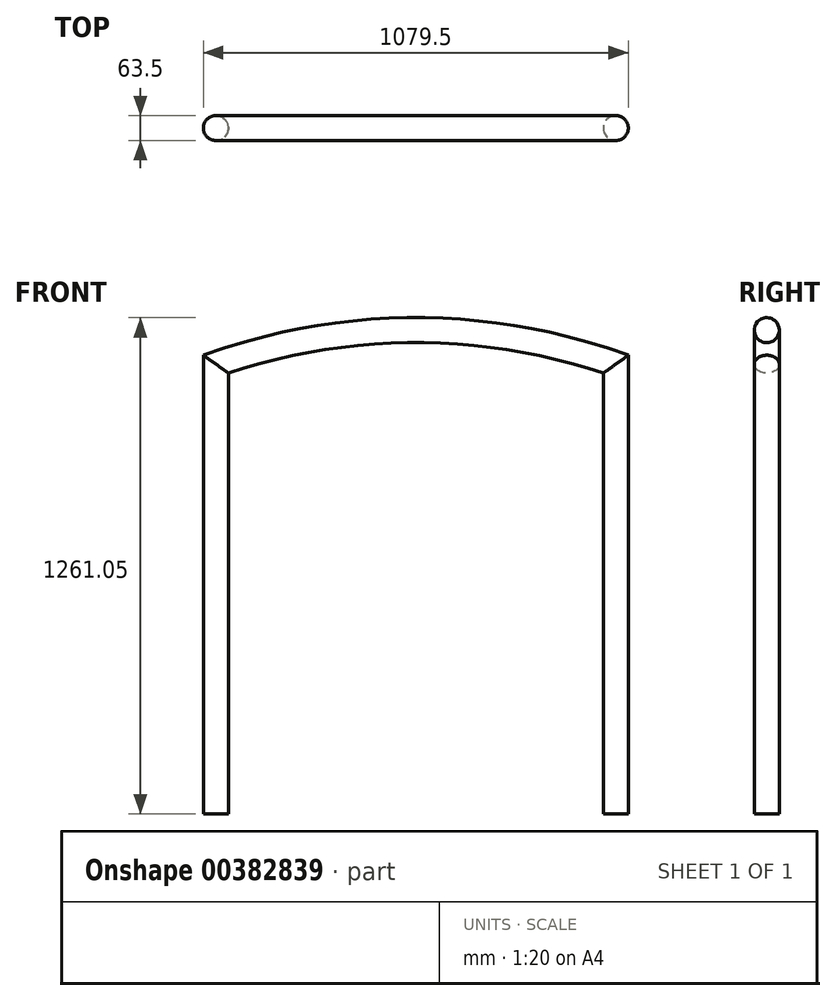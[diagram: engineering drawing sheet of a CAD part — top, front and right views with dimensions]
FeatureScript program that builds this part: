
annotation { "Feature Type Name" : "Feature", "Feature Type Description" : "" }
export const myFeature = defineFeature(function(context is Context, id is Id, definition is map)
    precondition{}
    {
        {
            var Q0;
            Q0=qCreatedBy(makeId("Front.planeOp"),FACE);
            var sketch = newSketch(context, id + "F0", { "sketchPlane" : qUnion([Q0])});
            skLineSegment(sketch, "E0", {"start": v(583.19, -789.06) * mm, "end": v(583.19, 353.94) * mm});
            skLineSegment(sketch, "E1", {"start": v(-432.81, -789.06) * mm, "end": v(-432.81, 353.94) * mm});
            skArc(sketch, "E2", {"start": v(583.19, 353.94) * mm, "mid": v(75.19, 440.24) * mm, "end": v(-432.81, 353.94) * mm});
            skSolve(sketch);
        }
        {
            var Q0;
            Q0=sQuery(id+"F0.wireOp",VERTEX,"E0.start");
            var Q1;
            Q1=sQuery(id+"F0.wireOp",EDGE,"E0");
            cPlane(context, id + "F1", {"entities" : qUnion([Q0, Q1]), "cplaneType" : CPlaneType.LINE_POINT, "offset" : 25.4 * mm, "width" : 152.4 * mm, "height" : 152.4 * mm});
        }
        {
            var Q0;
            Q0=qCreatedBy(id+"F1.planeOp",FACE);
            var sketch = newSketch(context, id + "F2", { "sketchPlane" : qUnion([Q0])});
            skPoint(sketch, "E3.0", {"position": v(583.19, 0) * mm});
            skCircle(sketch, "E4", {"center": v(583.19, 0) * mm, "radius": 31.75 * mm});
            skSolve(sketch);
        }
        {
            var Q0;
            Q0=makeQuery(id+"F2.imprint","IMPRINT",FACE,{"disambiguationData":[TD([[makeQuery(id+"F2.imprint","IMPRINT",EDGE,{"derivedFrom":sQuery(id+"F2.wireOp",EDGE,"E4")}),1.0]])]});
            var Q1;
            Q1=sQuery(id+"F0.wireOp",EDGE,"E0");
            var Q2;
            Q2=sQuery(id+"F0.wireOp",EDGE,"E2");
            var Q3;
            Q3=sQuery(id+"F0.wireOp",EDGE,"E1");
            sweep(context, id + "F3", {"profiles" : qUnion([Q0]), "path" : qUnion([Q1, Q2, Q3])});
        }
    });
